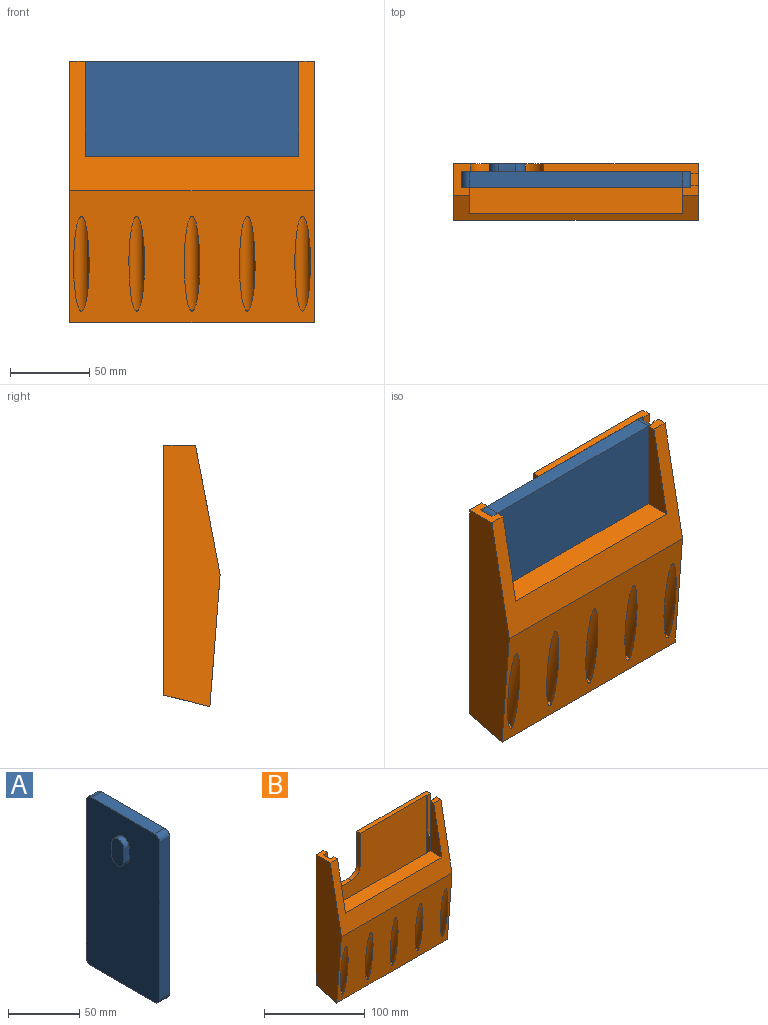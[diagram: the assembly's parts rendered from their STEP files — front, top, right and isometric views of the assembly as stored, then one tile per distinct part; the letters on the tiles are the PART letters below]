
ASSEMBLY  parts=2 mates=1
PART A: 15 faces, bbox 15x73x145 mm
  f0: plane 145x73mm, normal (-1,0,0), area 10318.4mm2, adj f1,f2,f4,f5,f6,f7,f8,f9
  f1: plane 63x10mm, normal (0,0,1), area 630mm2, adj f0,f3,f12,f14
  f2: plane 63x10mm, normal (0,0,-1), area 630mm2, adj f0,f3,f11,f13
  f3: plane 145x73mm, normal (1,0,0), area 10563.5mm2, adj f1,f2,f4,f5,f11,f12,f13,f14
  f4: plane 135x10mm, normal (0,-1,0), area 1350mm2, adj f0,f3,f13,f14
  f5: plane 135x10mm, normal (0,1,0), area 1350mm2, adj f0,f3,f11,f12
  f6: cylinder r=6mm len=12mm, axis (1,0,0), area 94.2mm2, adj f0,f7,f9,f10
  f7: plane 11x5mm, normal (0,1,0), area 55mm2, adj f0,f6,f8,f10
  f8: cylinder r=6mm len=12mm, axis (1,0,0), area 94.2mm2, adj f0,f7,f9,f10
  f9: plane 11x5mm, normal (0,-1,0), area 55mm2, adj f0,f6,f8,f10
  f10: plane 23x12mm, normal (-1,0,0), area 245.1mm2, adj f6,f7,f8,f9
  f11: cylinder r=5mm len=10mm, axis (1,0,0), area 78.5mm2, adj f0,f2,f3,f5
  f12: cylinder r=5mm len=10mm, axis (-1,0,0), area 78.5mm2, adj f0,f1,f3,f5
  f13: cylinder r=5mm len=10mm, axis (-1,0,0), area 78.5mm2, adj f0,f2,f3,f4
  f14: cylinder r=5mm len=10mm, axis (1,0,0), area 78.5mm2, adj f0,f1,f3,f4
PART B: 40 faces, bbox 155x44.1x165.3 mm
  f0: plane 155x81.9mm, normal (0,-0.98,0.19), area 4677.7mm2, adj f6,f7,f13,f14,f25,f26,f27,f28
  f1: cylinder r=5mm len=63.52mm, axis (0,0.24,-0.97), area 1047.1mm2, adj f28,f39
  f2: cylinder r=5mm len=63.52mm, axis (0,0.24,-0.97), area 1047.1mm2, adj f28,f37
  f3: cylinder r=5mm len=63.52mm, axis (0,0.24,-0.97), area 1047.1mm2, adj f28,f35
  f4: cylinder r=5mm len=63.52mm, axis (0,0.24,-0.97), area 1047.1mm2, adj f28,f33
  f5: cylinder r=5mm len=63.52mm, axis (0,0.24,-0.97), area 1047.1mm2, adj f28,f31
  f6: plane 10x6mm, normal (0,0,1), area 55mm2, adj f0,f11,f13,f16,f17,f26
  f7: plane 20x11mm, normal (0,0,1), area 155mm2, adj f0,f8,f11,f12,f14,f15,f22,f25
  f8: plane 158x155mm, normal (0,1,0), area 22205.8mm2, adj f7,f9,f13,f14,f20,f21,f22,f23
  f9: plane 98x6mm, normal (0,0,1), area 495mm2, adj f8,f12,f13,f16,f19,f23
  f10: plane 145x10mm, normal (0,0,1), area 1450mm2, adj f11,f12,f15,f16
  f11: plane 145x73mm, normal (0,1,0), area 2485mm2, adj f6,f7,f10,f15,f16,f25,f26,f27
  f12: plane 145x73mm, normal (0,-1,0), area 8300.8mm2, adj f7,f9,f10,f15,f16,f20,f21,f22
  f13: plane 165.28x35.61mm, normal (1,0,0), area 4485.3mm2, adj f0,f6,f8,f9,f17,f18,f19,f28
  f14: plane 165.28x35.61mm, normal (-1,0,0), area 4869.3mm2, adj f0,f7,f8,f28,f29
  f15: plane 73x10mm, normal (1,0,0), area 730mm2, adj f7,f10,f11,f12
  f16: plane 73x10mm, normal (-1,0,0), area 346mm2, adj f6,f9,f10,f11,f12,f17,f18,f19
  f17: plane 48x5mm, normal (0,1,0), area 240mm2, adj f6,f13,f16,f18
  f18: plane 8x5mm, normal (0,0,1), area 40mm2, adj f13,f16,f17,f19
  f19: plane 48x5mm, normal (0,-1,0), area 240mm2, adj f9,f13,f16,f18
  f20: plane 22x5mm, normal (0,0,1), area 110mm2, adj f8,f12,f21,f24
  f21: cylinder r=12mm len=12mm, axis (0,1,0), area 94.2mm2, adj f8,f12,f20,f22
  f22: plane 39x5mm, normal (1,0,0), area 195mm2, adj f7,f8,f12,f21
  f23: plane 39x5mm, normal (-1,0,0), area 195mm2, adj f8,f9,f12,f24
  f24: cylinder r=12mm len=12mm, axis (0,1,0), area 94.2mm2, adj f8,f12,f20,f23
  f25: plane 60x16.44mm, normal (1,0,0), area 643.1mm2, adj f0,f7,f11,f27
  f26: plane 60x16.44mm, normal (-1,0,0), area 643.1mm2, adj f0,f6,f11,f27
  f27: plane 135x16.44mm, normal (0,0,1), area 2219mm2, adj f0,f11,f25,f26
  f28: plane 155x83.37mm, normal (0,-1,-0.08), area 10600.8mm2, adj f0,f1,f2,f3,f4,f5,f13,f14
  f29: plane 155x29.1mm, normal (0,0.24,-0.97), area 4587.2mm2, adj f8,f13,f14,f28,f30,f32,f34,f36
  f30: cylinder r=2mm len=4.73mm, axis (0,0.24,-0.97), area 44mm2, adj f29,f31
  f31: plane 10x9.7mm, normal (0,-0.24,0.97), area 66mm2, adj f5,f30
  f32: cylinder r=2mm len=4.73mm, axis (0,0.24,-0.97), area 44mm2, adj f29,f33
  f33: plane 10x9.7mm, normal (0,-0.24,0.97), area 66mm2, adj f4,f32
  f34: cylinder r=2mm len=4.73mm, axis (0,0.24,-0.97), area 44mm2, adj f29,f35
  f35: plane 10x9.7mm, normal (0,-0.24,0.97), area 66mm2, adj f3,f34
  f36: cylinder r=2mm len=4.73mm, axis (0,0.24,-0.97), area 44mm2, adj f29,f37
  f37: plane 10x9.7mm, normal (0,-0.24,0.97), area 66mm2, adj f2,f36
  f38: cylinder r=2mm len=4.73mm, axis (0,0.24,-0.97), area 44mm2, adj f29,f39
  f39: plane 10x9.7mm, normal (0,-0.24,0.97), area 66mm2, adj f1,f38
PLACE A rot(axis=(0.58,-0.58,-0.58),120deg) t=(75.21,1.54,29.44)mm
PLACE B t=(-64.01,1.41,-7.06)mm
MATE planar A.f4 <-> B.f10  axis (0,0,1) through (-59.01,1.41,-43.56)mm
